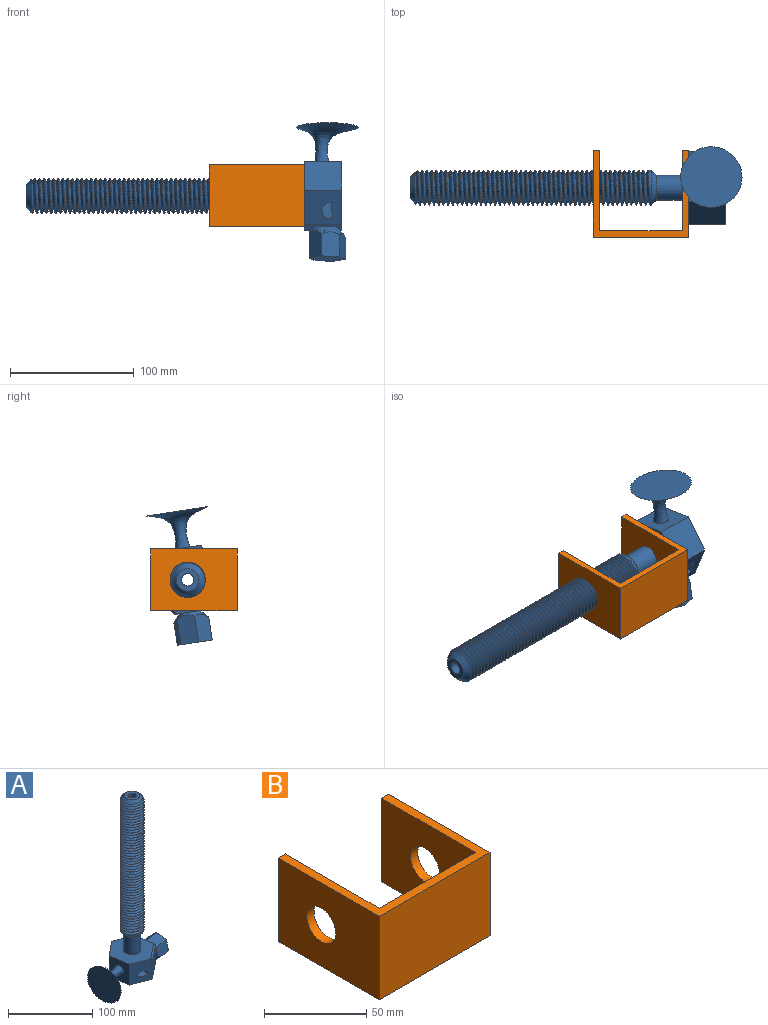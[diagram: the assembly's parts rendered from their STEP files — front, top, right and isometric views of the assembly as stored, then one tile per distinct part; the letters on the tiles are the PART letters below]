
ASSEMBLY  parts=2 mates=1
PART A: 36 faces, bbox 112.4x63.1x268.7 mm
  f0: plane 30x29.65mm, normal (-0.99,-0.15,0), area 785.3mm2, adj f3,f7,f8,f9,f35
  f1: plane 30.02x28.53mm, normal (0.99,0.15,0), area 618.2mm2, adj f2,f8,f9,f20,f21,f22,f24,f25
  f2: plane 30x27.96mm, normal (0.36,0.93,0), area 803.9mm2, adj f1,f7,f8,f9,f18,f19
  f3: plane 30.02x26.9mm, normal (-0.36,-0.93,0), area 769.1mm2, adj f0,f8,f9,f18,f19,f23,f24,f25
  f4: cylinder r=5mm len=255mm, axis (0,0,1), area 7826.7mm2, adj f9,f12,f18,f19
  f5: cone r=9.15mm half-angle=45deg, axis (0,0,-1), area 397.9mm2, adj f11,f12,f16,f17
  f6: plane 26x21.6mm, normal (0.63,-0.78,0), area 720mm2, adj f23,f24,f25,f26
  f7: plane 30x23.4mm, normal (-0.63,0.78,0), area 900mm2, adj f0,f2,f8,f9
  f8: plane 58.47x55.57mm, normal (0,0,1), area 1961.8mm2, adj f0,f1,f2,f3,f7,f10,f24
  f9: plane 58.47x55.57mm, normal (0,0,-1), area 2197.4mm2, adj f0,f1,f2,f3,f4,f7,f25
  f10: cylinder r=10mm len=25.85mm, axis (0,0,-1), area 1624.1mm2, adj f8,f13
  f11: cylinder r=14.15mm len=190mm, axis (0,0,-1), area 6171.9mm2, adj f5,f13,f14,f15,f16,f17
  f12: plane 18.3x18.3mm, normal (0,0,1), area 184.6mm2, adj f4,f5
  f13: cone r=14.15mm half-angle=45deg, axis (0,0,1), area 445.5mm2, adj f10,f11,f14,f15
  f14: plane 3.48x2.8mm, normal (0,1,0), area 4.9mm2, adj f11,f13,f15,f17
  f15: bspline ~192.06x33.26mm, area 13619.2mm2, adj f11,f13,f14,f16,f17
  f16: plane 2.8x2.23mm, normal (0,-1,0), area 1.1mm2, adj f5,f11,f15,f17
  f17: bspline ~191.74x33.26mm, area 12912.5mm2, adj f5,f11,f14,f15,f16
  f18: plane 53.66x31.63mm, normal (0.08,-0.03,1), area 616.7mm2, adj f2,f3,f4,f19
  f19: cylinder r=6.86mm len=53.4mm, axis (-0.36,-0.93,0), area 1182.1mm2, adj f2,f3,f4,f18
  f20: plane 1.79x1.31mm, normal (-0.81,0.59,0.03), area 0.3mm2, adj f1,f21,f22
  f21: cone r=7.9mm half-angle=45deg, axis (0.99,0.15,0), area 178mm2, adj f1,f20,f22,f27,f30,f31,f32
  f22: cone r=7.9mm half-angle=45deg, axis (0.99,0.15,0), area 301mm2, adj f1,f20,f21,f27,f28,f29,f30
  f23: cylinder r=2mm len=29.46mm, axis (0,0,-1), area 58.1mm2, adj f3,f6,f24,f25
  f24: cylinder r=2mm len=26.45mm, axis (-0.78,-0.63,0), area 94.9mm2, adj f1,f3,f6,f8,f23,f26
  f25: cylinder r=2mm len=26.45mm, axis (0.78,0.63,0), area 94.9mm2, adj f1,f3,f6,f9,f23,f26
  f26: cylinder r=2mm len=29.46mm, axis (0,0,1), area 58.1mm2, adj f1,f6,f24,f25
  f27: plane 20.83x14.67mm, normal (0.15,-0.97,0.21), area 298.4mm2, adj f21,f22,f28,f32,f33
  f28: plane 20.61x13.73mm, normal (0.1,-0.66,-0.74), area 288.3mm2, adj f22,f27,f29,f33
  f29: plane 20.9x16.82mm, normal (-0.05,0.3,-0.95), area 288.3mm2, adj f22,f28,f30,f33
  f30: plane 20.08x14.82mm, normal (-0.15,0.97,-0.21), area 288.9mm2, adj f21,f22,f29,f31,f33
  f31: plane 22.63x14.21mm, normal (-0.1,0.66,0.74), area 318mm2, adj f21,f30,f32,f33
  f32: plane 24.09x17.14mm, normal (0.05,-0.3,0.95), area 331.9mm2, adj f21,f27,f31,f33
  f33: plane 29.34x28.21mm, normal (0.99,0.15,0), area 584.6mm2, adj f27,f28,f29,f30,f31,f32
  f34: plane 49.58x49mm, normal (-0.99,-0.15,0), area 1928.5mm2, adj f35
  f35: bspline ~49.53x48.94mm, area 2668.3mm2, adj f0,f34
PART B: 12 faces, bbox 76.8x70x50 mm
  f0: plane 76.79x50mm, normal (0,-1,0), area 3839.5mm2, adj f1,f7,f8,f9
  f1: plane 70x50mm, normal (1,0,0), area 3185.8mm2, adj f0,f2,f8,f9,f11
  f2: plane 50x5mm, normal (0,1,0), area 250mm2, adj f1,f3,f8,f9
  f3: plane 65x50mm, normal (-1,0,0), area 2935.8mm2, adj f2,f4,f8,f9,f11
  f4: plane 66.79x50mm, normal (0,1,0), area 3339.5mm2, adj f3,f5,f8,f9
  f5: plane 65x50mm, normal (1,0,0), area 2935.8mm2, adj f4,f6,f8,f9,f10
  f6: plane 50x5mm, normal (0,1,0), area 250mm2, adj f5,f7,f8,f9
  f7: plane 70x50mm, normal (-1,0,0), area 3185.8mm2, adj f0,f6,f8,f9,f10
  f8: plane 76.79x70mm, normal (0,0,1), area 1034mm2, adj f0,f1,f2,f3,f4,f5,f6,f7
  f9: plane 76.79x70mm, normal (0,0,-1), area 1034mm2, adj f0,f1,f2,f3,f4,f5,f6,f7
  f10: cylinder r=10mm len=20mm, axis (-1,0,0), area 314.2mm2, adj f5,f7
  f11: cylinder r=10mm len=20mm, axis (-1,0,0), area 314.2mm2, adj f1,f3
PLACE A rot(axis=(0.71,0,-0.71),180deg) t=(-37.41,-25.53,94.01)mm
PLACE B t=(-105.81,-65.53,69.01)mm
MATE fastened A.f10 <-> B.f10  axis (-1,0,0) through (-67.41,-25.53,94.01)mm
